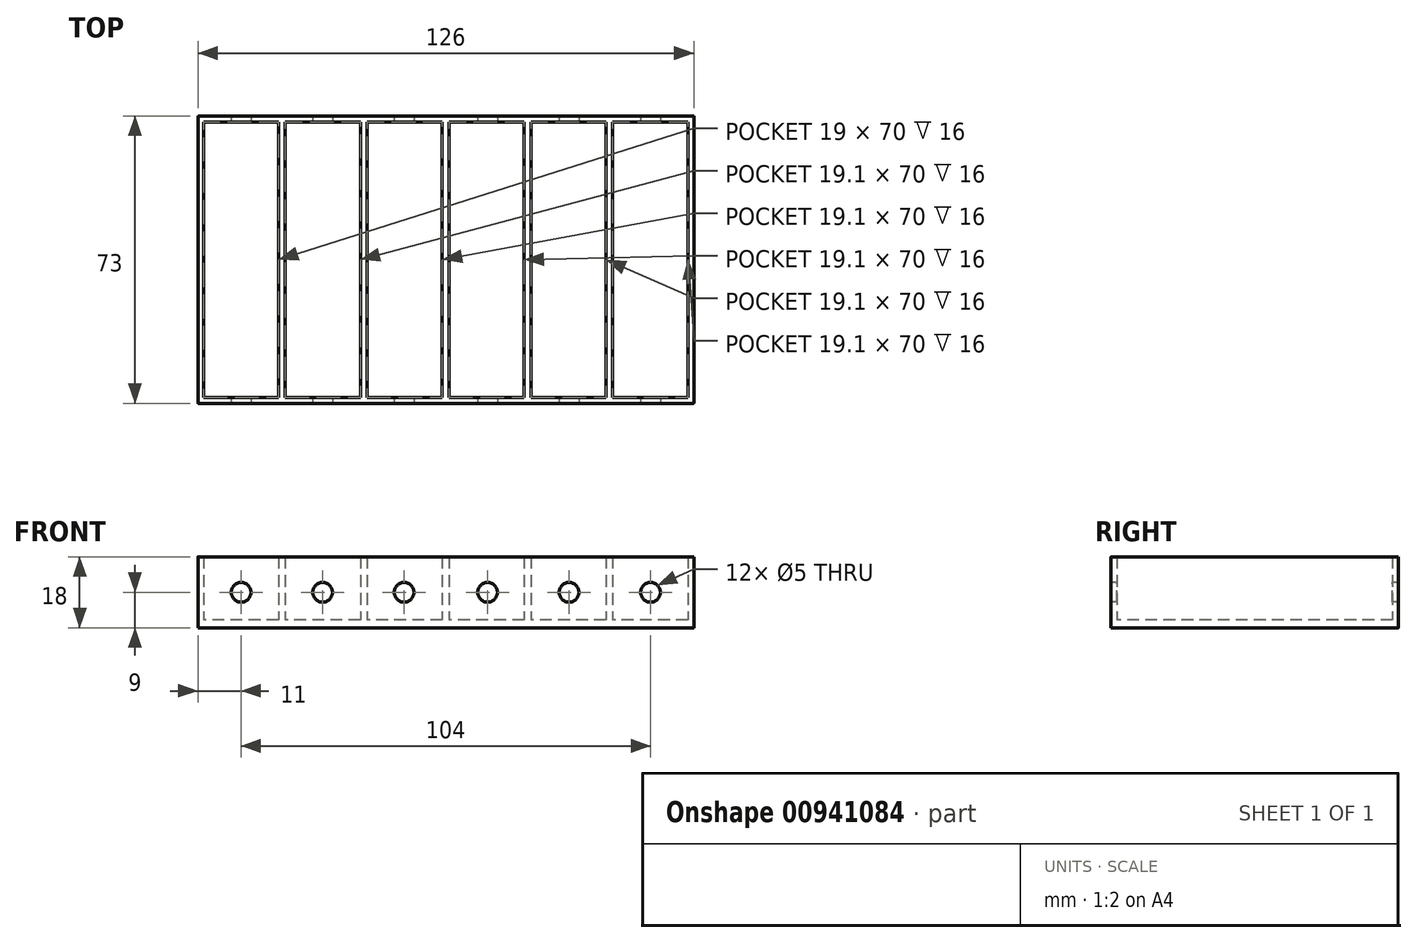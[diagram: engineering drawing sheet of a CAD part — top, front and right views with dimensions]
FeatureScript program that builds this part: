
annotation { "Feature Type Name" : "Feature", "Feature Type Description" : "" }
export const myFeature = defineFeature(function(context is Context, id is Id, definition is map)
    precondition{}
    {
        {
            var Q0;
            Q0=qCreatedBy(makeId("Top.planeOp"),FACE);
            var sketch = newSketch(context, id + "F0", { "sketchPlane" : qUnion([Q0])});
            skLineSegment(sketch, "E0.bottom", {"start": v(63, 36.5) * mm, "end": v(-63, 36.5) * mm});
            skLineSegment(sketch, "E0.top", {"start": v(63, -36.5) * mm, "end": v(-63, -36.5) * mm});
            skLineSegment(sketch, "E0.left", {"start": v(63, 36.5) * mm, "end": v(63, -36.5) * mm});
            skLineSegment(sketch, "E0.right", {"start": v(-63, 36.5) * mm, "end": v(-63, -36.5) * mm});
            skPoint(sketch, "E0.middle", {"position": v(0, 0) * mm});
            skSolve(sketch);
        }
        {
            var Q0;
            Q0=qSketchRegion(id+"F0",true);
            extrude(context, id + "F1", {"entities" : qUnion([Q0]), "depth" : 2 * mm, "offsetDistance" : 25 * mm});
        }
        {
            var Q0;
            Q0=makeQuery(id+"F1.opExtrude","CAP_FACE",FACE,{"disambiguationData":[OSD([sQuery(id+"F0.wireOp",EDGE,"E0.bottom"),sQuery(id+"F0.wireOp",EDGE,"E0.top"),sQuery(id+"F0.wireOp",EDGE,"E0.left"),sQuery(id+"F0.wireOp",EDGE,"E0.right")])],"isStart":false});
            var sketch = newSketch(context, id + "F2", { "sketchPlane" : qUnion([Q0])});
            skLineSegment(sketch, "E1.0", {"start": v(61.5, 35) * mm, "end": v(-61.5, 35) * mm});
            skLineSegment(sketch, "E1.1", {"start": v(61.5, 35) * mm, "end": v(61.5, -35) * mm});
            skLineSegment(sketch, "E1.2", {"start": v(61.5, -35) * mm, "end": v(-61.5, -35) * mm});
            skLineSegment(sketch, "E1.3", {"start": v(-61.5, 35) * mm, "end": v(-61.5, -35) * mm});
            skLineSegment(sketch, "E2.0", {"start": v(63, 36.5) * mm, "end": v(-63, 36.5) * mm});
            skLineSegment(sketch, "E2.1", {"start": v(63, 36.5) * mm, "end": v(63, -36.5) * mm});
            skLineSegment(sketch, "E2.2", {"start": v(63, -36.5) * mm, "end": v(-63, -36.5) * mm});
            skLineSegment(sketch, "E2.3", {"start": v(-63, 36.5) * mm, "end": v(-63, -36.5) * mm});
            skLineSegment(sketch, "E3.0", {"start": v(-42.5, 37.5) * mm, "end": v(-42.5, -37.5) * mm});
            skLineSegment(sketch, "E4.0", {"start": v(-40.8, 37.5) * mm, "end": v(-40.8, -37.5) * mm});
            skLineSegment(sketch, "E5.0", {"start": v(42.4, 37.5) * mm, "end": v(42.4, -37.5) * mm});
            skLineSegment(sketch, "E6.0", {"start": v(40.7, 37.5) * mm, "end": v(40.7, -37.5) * mm});
            skLineSegment(sketch, "E7.0", {"start": v(21.6, 37.5) * mm, "end": v(21.6, -37.5) * mm});
            skLineSegment(sketch, "E8.0", {"start": v(19.9, 37.5) * mm, "end": v(19.9, -37.5) * mm});
            skLineSegment(sketch, "E9.0", {"start": v(0.8, 37.5) * mm, "end": v(0.8, -37.5) * mm});
            skLineSegment(sketch, "E10.0", {"start": v(-0.9, 37.5) * mm, "end": v(-0.9, -37.5) * mm});
            skLineSegment(sketch, "E11.0", {"start": v(-20, 37.5) * mm, "end": v(-20, -37.5) * mm});
            skLineSegment(sketch, "E12.0", {"start": v(-21.7, 37.5) * mm, "end": v(-21.7, -37.5) * mm});
            skSolve(sketch);
        }
        {
            var Q0;
            Q0=qSketchRegion(id+"F2",true);
            var Q1;
            {var subQ0=sQuery(id+"F2.wireOp",EDGE,"E3.0");Q1=makeQuery(id+"F2.imprint","IMPRINT",FACE,{"disambiguationData":[TD([[makeQuery(id+"F2.imprint","IMPRINT",EDGE,{"derivedFrom":subQ0}),1.0]])]});}
            var Q2;
            {var subQ0=sQuery(id+"F2.wireOp",EDGE,"E11.0");Q2=makeQuery(id+"F2.imprint","IMPRINT",FACE,{"disambiguationData":[TD([[makeQuery(id+"F2.imprint","IMPRINT",EDGE,{"derivedFrom":subQ0}),-1.0]])]});}
            var Q3;
            {var subQ0=sQuery(id+"F2.wireOp",EDGE,"E9.0");Q3=makeQuery(id+"F2.imprint","IMPRINT",FACE,{"disambiguationData":[TD([[makeQuery(id+"F2.imprint","IMPRINT",EDGE,{"derivedFrom":subQ0}),-1.0]])]});}
            var Q4;
            {var subQ0=sQuery(id+"F2.wireOp",EDGE,"E7.0");Q4=makeQuery(id+"F2.imprint","IMPRINT",FACE,{"disambiguationData":[TD([[makeQuery(id+"F2.imprint","IMPRINT",EDGE,{"derivedFrom":subQ0}),-1.0]])]});}
            var Q5;
            {var subQ0=sQuery(id+"F2.wireOp",EDGE,"E5.0");Q5=makeQuery(id+"F2.imprint","IMPRINT",FACE,{"disambiguationData":[TD([[makeQuery(id+"F2.imprint","IMPRINT",EDGE,{"derivedFrom":subQ0}),-1.0]])]});}
            extrude(context, id + "F3", {"entities" : qUnion([Q0, Q1, Q2, Q3, Q4, Q5]), "operationType" : NewBodyOperationType.ADD, "depth" : 16 * mm, "offsetDistance" : 25 * mm});
        }
        {
            var Q0;
            Q0=makeQuery(id+"F3.boolean.opBoolean","MERGE",FACE,{"derivedFrom":[makeQuery(id+"F1.opExtrude","SWEPT_FACE",FACE,{"disambiguationData":[OSD([sQuery(id+"F0.wireOp",EDGE,"E0.top")])]}),makeQuery(id+"F3.opExtrude","SWEPT_FACE",FACE,{"disambiguationData":[OSD([sQuery(id+"F2.wireOp",EDGE,"E2.2")])]})]});
            var sketch = newSketch(context, id + "F4", { "sketchPlane" : qUnion([Q0])});
            skLineSegment(sketch, "E13", {"start": v(-63, 9) * mm, "end": v(63, 9) * mm});
            skCircle(sketch, "E14", {"center": v(-52, 9) * mm, "radius": 2.5 * mm});
            skCircle(sketch, "E15", {"center": v(-31.3, 9) * mm, "radius": 2.5 * mm});
            skCircle(sketch, "E16", {"center": v(-10.6, 9) * mm, "radius": 2.5 * mm});
            skCircle(sketch, "E17.MirrorC", {"center": v(10.6, 9) * mm, "radius": 2.5 * mm});
            skCircle(sketch, "E18.MirrorC", {"center": v(31.3, 9) * mm, "radius": 2.5 * mm});
            skCircle(sketch, "E19.MirrorC", {"center": v(52, 9) * mm, "radius": 2.5 * mm});
            skSolve(sketch);
        }
        {
            var Q0;
            Q0=qSketchRegion(id+"F4",true);
            extrude(context, id + "F5", {"entities" : qUnion([Q0]), "operationType" : NewBodyOperationType.REMOVE, "oppositeDirection" : true, "depth" : 100 * mm, "offsetDistance" : 25 * mm});
        }
        {
            var Q0;
            Q0=makeQuery(id+"F3.boolean.opBoolean","MERGE",EDGE,{"derivedFrom":[makeQuery(id+"F1.opExtrude","SWEPT_EDGE",EDGE,{"disambiguationData":[OSD([sQuery(id+"F0.wireOp",EDGE,"E0.top"),sQuery(id+"F0.wireOp",EDGE,"E0.right")])]}),makeQuery(id+"F3.opExtrude","SWEPT_EDGE",EDGE,{"disambiguationData":[OSD([sQuery(id+"F2.wireOp",EDGE,"E2.2"),sQuery(id+"F2.wireOp",EDGE,"E2.3")])]})]});
            var Q1;
            Q1=makeQuery(id+"F3.boolean.opBoolean","MERGE",EDGE,{"derivedFrom":[makeQuery(id+"F1.opExtrude","SWEPT_EDGE",EDGE,{"disambiguationData":[OSD([sQuery(id+"F0.wireOp",EDGE,"E0.top"),sQuery(id+"F0.wireOp",EDGE,"E0.left")])]}),makeQuery(id+"F3.opExtrude","SWEPT_EDGE",EDGE,{"disambiguationData":[OSD([sQuery(id+"F2.wireOp",EDGE,"E2.1"),sQuery(id+"F2.wireOp",EDGE,"E2.2")])]})]});
            var Q2;
            Q2=makeQuery(id+"F3.boolean.opBoolean","MERGE",EDGE,{"derivedFrom":[makeQuery(id+"F1.opExtrude","SWEPT_EDGE",EDGE,{"disambiguationData":[OSD([sQuery(id+"F0.wireOp",EDGE,"E0.bottom"),sQuery(id+"F0.wireOp",EDGE,"E0.left")])]}),makeQuery(id+"F3.opExtrude","SWEPT_EDGE",EDGE,{"disambiguationData":[OSD([sQuery(id+"F2.wireOp",EDGE,"E2.0"),sQuery(id+"F2.wireOp",EDGE,"E2.1")])]})]});
            var Q3;
            Q3=makeQuery(id+"F3.boolean.opBoolean","MERGE",EDGE,{"derivedFrom":[makeQuery(id+"F1.opExtrude","SWEPT_EDGE",EDGE,{"disambiguationData":[OSD([sQuery(id+"F0.wireOp",EDGE,"E0.bottom"),sQuery(id+"F0.wireOp",EDGE,"E0.right")])]}),makeQuery(id+"F3.opExtrude","SWEPT_EDGE",EDGE,{"disambiguationData":[OSD([sQuery(id+"F2.wireOp",EDGE,"E2.0"),sQuery(id+"F2.wireOp",EDGE,"E2.3")])]})]});
            fillet(context, id + "F6", {"entities" : qUnion([Q0, Q1, Q2, Q3]), "radius" : .1 * mm, "tangentPropagation" : true, "allowEdgeOverflow" : false});
        }
    });
